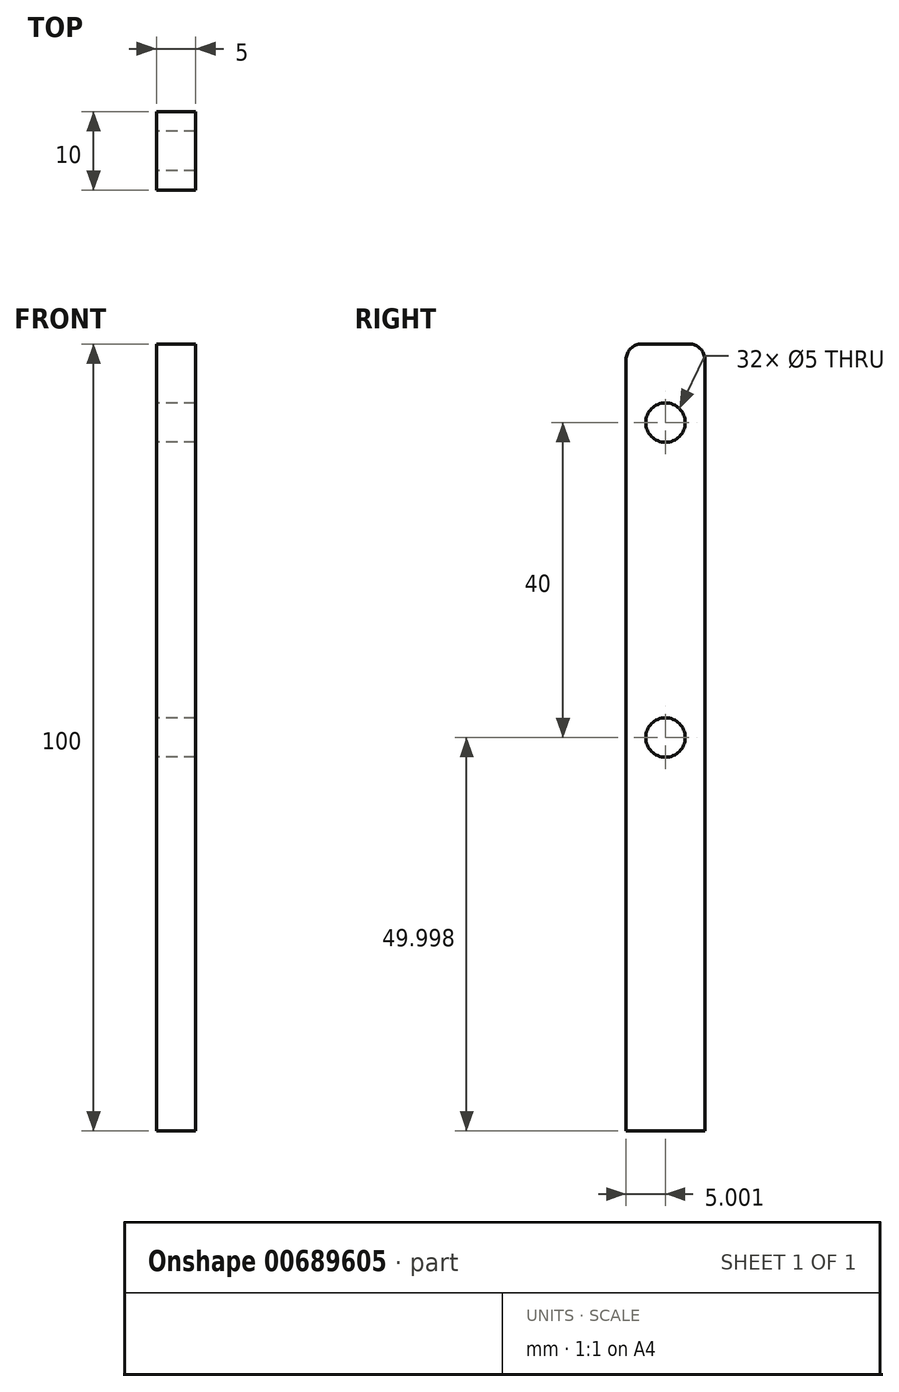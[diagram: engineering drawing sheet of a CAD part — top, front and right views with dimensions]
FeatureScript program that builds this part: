
annotation { "Feature Type Name" : "Feature", "Feature Type Description" : "" }
export const myFeature = defineFeature(function(context is Context, id is Id, definition is map)
    precondition{}
    {
        {
            var Q0;
            Q0=qCreatedBy(makeId("Right.planeOp"),FACE);
            var sketch = newSketch(context, id + "F0", { "sketchPlane" : qUnion([Q0])});
            skLineSegment(sketch, "E0.bottom", {"start": v(-31.02, 2.86) * mm, "end": v(-41.02, 2.86) * mm});
            skLineSegment(sketch, "E0.top", {"start": v(-33.02, 102.86) * mm, "end": v(-39.02, 102.86) * mm});
            skLineSegment(sketch, "E0.left", {"start": v(-31.02, 2.86) * mm, "end": v(-31.02, 100.86) * mm});
            skLineSegment(sketch, "E0.right", {"start": v(-41.02, 2.86) * mm, "end": v(-41.02, 100.86) * mm});
            skPoint(sketch, "E0.middle", {"position": v(-36.02, 52.86) * mm});
            skCircle(sketch, "E1", {"center": v(-36.02, 92.86) * mm, "radius": 2.5 * mm});
            skPoint(sketch, "E2.visualSharp", {"position": v(-41.02, 102.86) * mm});
            skArc(sketch, "E2.filletArc", {"start": v(-39.02, 102.86) * mm, "mid": v(-40.43, 102.27) * mm, "end": v(-41.02, 100.86) * mm});
            skPoint(sketch, "E3.visualSharp", {"position": v(-31.02, 102.86) * mm});
            skArc(sketch, "E3.filletArc", {"start": v(-31.02, 100.86) * mm, "mid": v(-31.6, 102.27) * mm, "end": v(-33.02, 102.86) * mm});
            skCircle(sketch, "E4", {"center": v(-36.02, 52.86) * mm, "radius": 2.5 * mm});
            skSolve(sketch);
        }
        {
            var Q0;
            Q0=makeQuery(id+"F0.imprint","IMPRINT",FACE,{"disambiguationData":[TD([[makeQuery(id+"F0.imprint","IMPRINT",EDGE,{"derivedFrom":sQuery(id+"F0.wireOp",EDGE,"E0.bottom")}),-1.0]])]});
            extrude(context, id + "F1", {"entities" : qUnion([Q0]), "depth" : 5 * mm, "offsetDistance" : 25 * mm});
        }
    });
